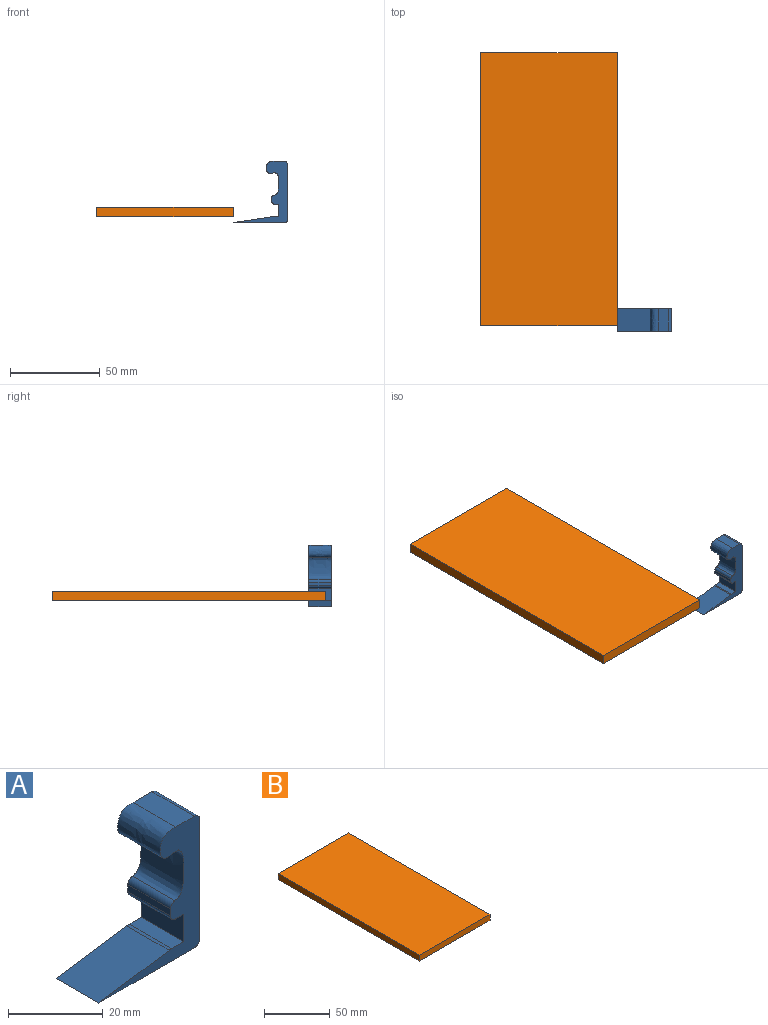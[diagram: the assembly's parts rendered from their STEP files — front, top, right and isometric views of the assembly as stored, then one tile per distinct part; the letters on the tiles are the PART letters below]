
ASSEMBLY  parts=2 mates=1
PART A: 19 faces, bbox 30.2x12.7x34.2 mm
  f0: plane 12.7x0.25mm, normal (-1,0,0), area 3.2mm2, adj f1,f15,f16,f17
  f1: extruded ~12.7x12.3mm, area 179.5mm2, adj f0,f2,f16,f17
  f2: cylinder r=1.59mm len=12.7mm, axis (0,-1,0), area 28.1mm2, adj f1,f3,f16,f17
  f3: plane 12.7x1.75mm, normal (-1,0,0), area 22.3mm2, adj f2,f4,f16,f17
  f4: cylinder r=1.59mm len=12.7mm, axis (0,-1,0), area 31.7mm2, adj f3,f5,f16,f17
  f5: plane 12.7x2.41mm, normal (0,0,-1), area 30.7mm2, adj f4,f6,f16,f17
  f6: plane 12.7x7.09mm, normal (-1,0,0), area 90mm2, adj f5,f7,f16,f17
  f7: plane 12.7x3.63mm, normal (0,0,1), area 46.1mm2, adj f6,f16,f17,f18
  f8: plane 21.03x12.7mm, normal (-0.15,0,0.99), area 270mm2, adj f9,f16,f17,f18
  f9: plane 28.58x12.7mm, normal (0,0,-1), area 362.9mm2, adj f8,f10,f16,f17
  f10: cylinder r=1.59mm len=12.7mm, axis (0,-1,0), area 31.7mm2, adj f9,f11,f16,f17
  f11: plane 30.9x12.7mm, normal (1,0,0), area 392.4mm2, adj f10,f12,f16,f17
  f12: cylinder r=1.59mm len=12.7mm, axis (0,-1,0), area 31.7mm2, adj f11,f13,f16,f17
  f13: plane 12.7x5.65mm, normal (0,0,1), area 71.7mm2, adj f12,f14,f16,f17
  f14: extruded ~12.7x6.63mm, area 162.4mm2, adj f13,f15,f16,f17
  f15: plane 12.7x1.5mm, normal (0,0,-1), area 19mm2, adj f0,f14,f16,f17
  f16: plane 34.19x30.16mm, normal (0,1,0), area 273.1mm2, adj f0,f1,f2,f3,f4,f5,f6,f7
  f17: plane 34.19x30.16mm, normal (0,-1,0), area 273.1mm2, adj f0,f1,f2,f3,f4,f5,f6,f7
  f18: cylinder r=5.08mm len=12.7mm, axis (0,1,0), area 9.5mm2, adj f7,f8,f16,f17
PART B: 6 faces, bbox 76.2x152.4x5.5 mm
  f0: plane 152.4x76.2mm, normal (0,0,-1), area 11612.9mm2, adj f1,f3,f4,f5
  f1: plane 152.4x5.5mm, normal (1,0,0), area 838.1mm2, adj f0,f2,f4,f5
  f2: plane 152.4x76.2mm, normal (0,0,1), area 11612.9mm2, adj f1,f3,f4,f5
  f3: plane 152.4x5.5mm, normal (-1,0,0), area 838.1mm2, adj f0,f2,f4,f5
  f4: plane 76.2x5.5mm, normal (0,1,0), area 419mm2, adj f0,f1,f2,f3
  f5: plane 76.2x5.5mm, normal (0,-1,0), area 419mm2, adj f0,f1,f2,f3
PLACE A t=(23.35,-81.77,1.77)mm
PLACE B t=(-2.05,-78.63,1.77)mm
MATE slider A.f17 <-> B.f5  axis (0,-1,0) through (23.35,-81.77,1.77)mm
